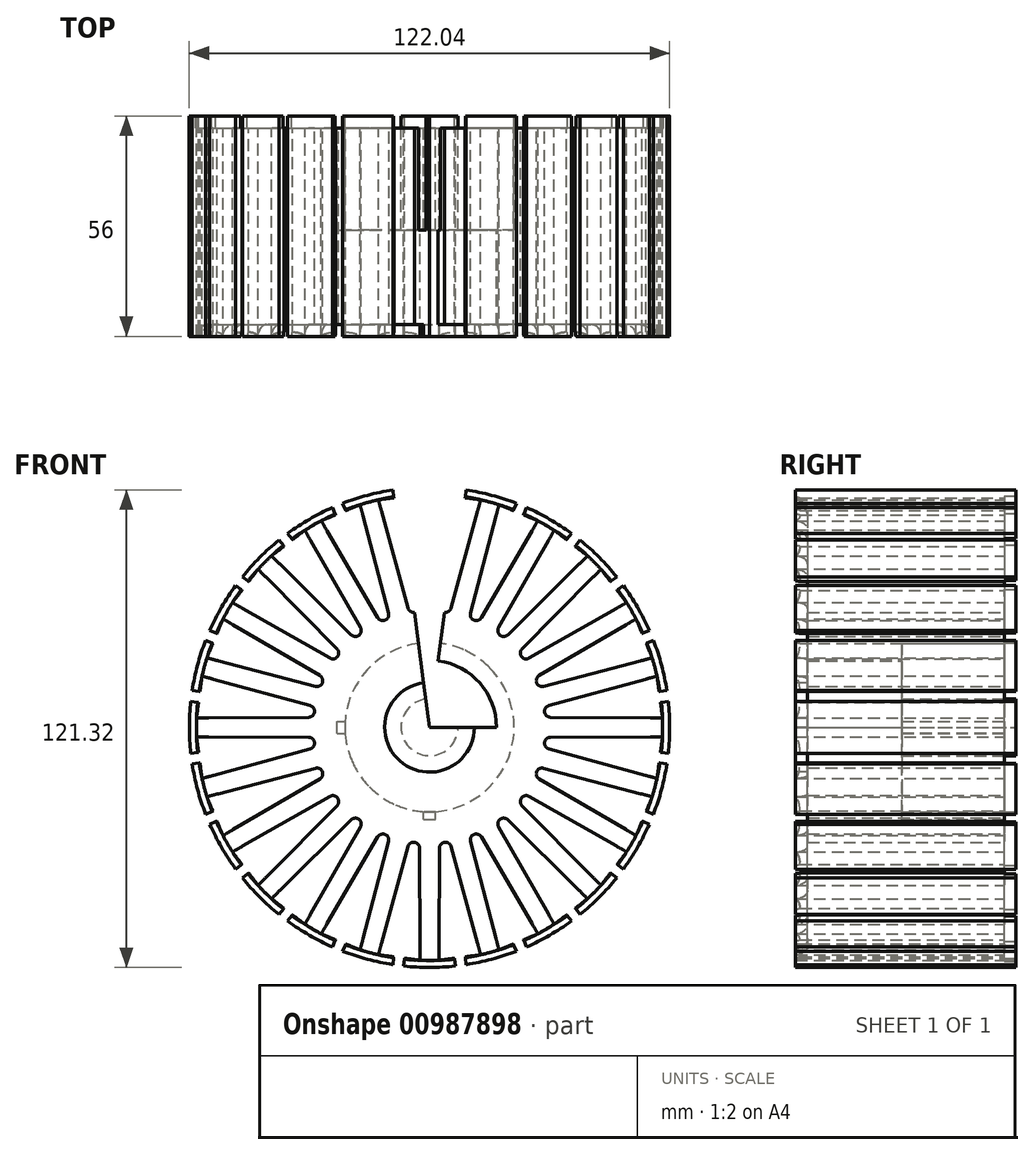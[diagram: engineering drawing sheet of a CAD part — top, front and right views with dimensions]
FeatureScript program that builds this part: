
annotation { "Feature Type Name" : "Feature", "Feature Type Description" : "" }
export const myFeature = defineFeature(function(context is Context, id is Id, definition is map)
    precondition{}
    {
        {
            var Q0;
            Q0=qCreatedBy(makeId("Front.planeOp"),FACE);
            var sketch = newSketch(context, id + "F0", { "sketchPlane" : qUnion([Q0])});
            skCircle(sketch, "E0", {"center": v(0, 0) * mm, "radius": 17 * mm});
            skLineSegment(sketch, "E1", {"start": v(0, 0) * mm, "end": v(0, 0) * mm});
            skLineSegment(sketch, "E2.MirrorCS", {"start": v(-63, 0) * mm, "end": v(-17, 0) * mm});
            skLineSegment(sketch, "E3.MirrorCS", {"start": v(-61, 5.5) * mm, "end": v(-30.77, 1.49) * mm});
            skLineSegment(sketch, "E4.MirrorCS", {"start": v(-61, -5.5) * mm, "end": v(-30.77, -1.49) * mm});
            skArc(sketch, "E5.MirrorCS", {"start": v(-30.77, 1.49) * mm, "mid": v(-29.47, 0) * mm, "end": v(-30.77, -1.49) * mm});
            skLineSegment(sketch, "E6.MirrorCS", {"start": v(-61, 1.38) * mm, "end": v(-61, 5.5) * mm});
            skLineSegment(sketch, "E7.MirrorCS", {"start": v(-63, 1.38) * mm, "end": v(-61, 1.38) * mm});
            skLineSegment(sketch, "E8.MirrorCS", {"start": v(-63, -1.38) * mm, "end": v(-61, -1.38) * mm});
            skLineSegment(sketch, "E9.MirrorCS", {"start": v(-61, -1.38) * mm, "end": v(-61, -5.5) * mm});
            skText(sketch, "E10", { "text": "correct", "fontName": "OpenSans-Regular.ttf"});
            skLineSegment(sketch, "E11.trimOffspring", {"start": v(-17, 0) * mm, "end": v(-26.3, 0) * mm});
            skLineSegment(sketch, "E12", {"start": v(0, 0) * mm, "end": v(54.99, 0) * mm});
            skLineSegment(sketch, "E13.MirrorCS", {"start": v(60.3, 9.33) * mm, "end": v(59.78, 13.26) * mm});
            skLineSegment(sketch, "E14.MirrorCS", {"start": v(60.66, 6.6) * mm, "end": v(61.17, 2.66) * mm});
            skLineSegment(sketch, "E15.MirrorCS", {"start": v(61.17, 2.66) * mm, "end": v(30.7, 2.54) * mm});
            skLineSegment(sketch, "E16.MirrorCS", {"start": v(59.78, 13.26) * mm, "end": v(30.32, 5.5) * mm});
            skArc(sketch, "E17.MirrorCS", {"start": v(30.32, 5.5) * mm, "mid": v(29.22, 3.85) * mm, "end": v(30.7, 2.54) * mm});
            skLineSegment(sketch, "E18.MirrorCS", {"start": v(62.46, 8.23) * mm, "end": v(0, 0) * mm});
            skLineSegment(sketch, "E19.MirrorCS", {"start": v(62.28, 9.6) * mm, "end": v(62.64, 6.86) * mm});
            skLineSegment(sketch, "E20.MirrorCS", {"start": v(62.64, 6.86) * mm, "end": v(60.66, 6.6) * mm});
            skLineSegment(sketch, "E21.MirrorCS", {"start": v(62.28, 9.6) * mm, "end": v(60.3, 9.33) * mm});
            skLineSegment(sketch, "E22.MirrorCS", {"start": v(0, 0) * mm, "end": v(-7.96, 60.48) * mm});
            skArc(sketch, "E23.MirrorCS", {"start": v(-5.5, 30.32) * mm, "mid": v(-3.85, 29.22) * mm, "end": v(-2.54, 30.71) * mm});
            skLineSegment(sketch, "E24.MirrorCS", {"start": v(-13, 57.8) * mm, "end": v(-5.5, 30.32) * mm});
            skLineSegment(sketch, "E25.MirrorCS", {"start": v(-2.4, 59.2) * mm, "end": v(-2.54, 30.71) * mm});
            skLineSegment(sketch, "E26.MirrorCS", {"start": v(-9.07, 58.32) * mm, "end": v(-13, 57.8) * mm});
            skLineSegment(sketch, "E27.MirrorCS", {"start": v(-9.33, 60.3) * mm, "end": v(-9.07, 58.32) * mm});
            skLineSegment(sketch, "E28.MirrorCS", {"start": v(-6.6, 60.66) * mm, "end": v(-6.33, 58.68) * mm});
            skLineSegment(sketch, "E29.MirrorCS", {"start": v(-6.33, 58.68) * mm, "end": v(-2.4, 59.2) * mm});
            skLineSegment(sketch, "E30", {"start": v(0, 50.95) * mm, "end": v(0, 0) * mm});
            skLineSegment(sketch, "E31.MirrorCS", {"start": v(2.4, 59.2) * mm, "end": v(2.54, 30.71) * mm});
            skArc(sketch, "E32.MirrorCS", {"start": v(5.5, 30.32) * mm, "mid": v(3.85, 29.22) * mm, "end": v(2.54, 30.71) * mm});
            skLineSegment(sketch, "E33.MirrorCS", {"start": v(0, 0) * mm, "end": v(7.96, 60.48) * mm});
            skLineSegment(sketch, "E34.MirrorCS", {"start": v(13, 57.8) * mm, "end": v(5.5, 30.32) * mm});
            skLineSegment(sketch, "E35.MirrorCS", {"start": v(6.33, 58.68) * mm, "end": v(2.4, 59.2) * mm});
            skLineSegment(sketch, "E36.MirrorCS", {"start": v(9.33, 60.3) * mm, "end": v(9.07, 58.32) * mm});
            skLineSegment(sketch, "E37.MirrorCS", {"start": v(9.07, 58.32) * mm, "end": v(13, 57.8) * mm});
            skLineSegment(sketch, "E38.MirrorCS", {"start": v(6.6, 60.66) * mm, "end": v(6.33, 58.68) * mm});
            skArc(sketch, "E39", {"start": v(-6.6, 60.66) * mm, "mid": v(0, 61.02) * mm, "end": v(6.6, 60.66) * mm});
            const initialGuessF0  = {"E10": [-0.06317, -0.01425, 1, 0, 0.0042]};
            skSetInitialGuess(sketch, initialGuessF0);
            skSolve(sketch);
        }
        {
            var Q0;
            {var subQ0=sQuery(id+"F0.wireOp",EDGE,"E33.MirrorCS");var subQ1=sQuery(id+"F0.wireOp",EDGE,"E0");var subQ2=makeQuery(id+"F0.imprint","INTERSECT",VERTEX,{"derivedFrom":[subQ1,subQ0]});Q0=makeQuery(id+"F0.imprint","IMPRINT",FACE,{"disambiguationData":[TD([[makeQuery(id+"F0.imprint","IMPRINT",EDGE,{"disambiguationData":[TD([[subQ2,-1.0]])],"derivedFrom":subQ1}),-1.0]])]});}
            var Q1;
            {var subQ0=sQuery(id+"F0.wireOp",EDGE,"E30");var subQ1=sQuery(id+"F0.wireOp",EDGE,"E0");var subQ2=makeQuery(id+"F0.imprint","INTERSECT",VERTEX,{"derivedFrom":[subQ1,subQ0]});Q1=makeQuery(id+"F0.imprint","IMPRINT",FACE,{"disambiguationData":[TD([[makeQuery(id+"F0.imprint","IMPRINT",EDGE,{"disambiguationData":[TD([[subQ2,-1.0]])],"derivedFrom":subQ1}),-1.0]])]});}
            var Q2;
            {var subQ0=sQuery(id+"F0.wireOp",EDGE,"E18.MirrorCS");var subQ1=sQuery(id+"F0.wireOp",EDGE,"E0");var subQ2=makeQuery(id+"F0.imprint","INTERSECT",VERTEX,{"derivedFrom":[subQ1,subQ0]});Q2=makeQuery(id+"F0.imprint","IMPRINT",FACE,{"disambiguationData":[TD([[makeQuery(id+"F0.imprint","IMPRINT",EDGE,{"disambiguationData":[TD([[subQ2,-1.0]])],"derivedFrom":subQ1}),-1.0]])]});}
            var Q3;
            {var subQ0=sQuery(id+"F0.wireOp",EDGE,"E22.MirrorCS");var subQ1=sQuery(id+"F0.wireOp",EDGE,"E0");var subQ2=makeQuery(id+"F0.imprint","INTERSECT",VERTEX,{"derivedFrom":[subQ1,subQ0]});Q3=makeQuery(id+"F0.imprint","IMPRINT",FACE,{"disambiguationData":[TD([[makeQuery(id+"F0.imprint","IMPRINT",EDGE,{"disambiguationData":[TD([[subQ2,-1.0]])],"derivedFrom":subQ1}),-1.0]])]});}
            var Q4;
            {var subQ1=sQuery(id+"F0.wireOp",EDGE,"E0");var subQ5=makeQuery(id+"F0.imprint","INTERSECT",VERTEX,{"derivedFrom":[subQ1,sQuery(id+"F0.wireOp",EDGE,"E11.trimOffspring")]});Q4=makeQuery(id+"F0.imprint","IMPRINT",FACE,{"disambiguationData":[TD([[makeQuery(id+"F0.imprint","IMPRINT",EDGE,{"disambiguationData":[TD([[subQ5,1.0]])],"derivedFrom":subQ1}),1.0]])]});}
            var Q5;
            {var subQ7=sQuery(id+"F0.wireOp",EDGE,"E25.MirrorCS");Q5=makeQuery(id+"F0.imprint","IMPRINT",FACE,{"disambiguationData":[TD([[makeQuery(id+"F0.imprint","IMPRINT",EDGE,{"derivedFrom":subQ7}),1.0]])]});}
            extrude(context, id + "F1", {"entities" : qUnion([Q0, Q1, Q2, Q3, Q4, Q5]), "depth" : 56 * mm, "offsetDistance" : 25 * mm});
        }
        {
            var Q0;
            Q0=makeQuery(id+"F1.opExtrude","SWEPT_BODY",BODY,{"disambiguationData":[OSD([sQuery(id+"F0.wireOp",EDGE,"E0"),sQuery(id+"F0.wireOp",EDGE,"E22.MirrorCS"),sQuery(id+"F0.wireOp",EDGE,"E23.MirrorCS"),sQuery(id+"F0.wireOp",EDGE,"E25.MirrorCS"),sQuery(id+"F0.wireOp",EDGE,"E28.MirrorCS"),sQuery(id+"F0.wireOp",EDGE,"E29.MirrorCS"),sQuery(id+"F0.wireOp",EDGE,"E31.MirrorCS"),sQuery(id+"F0.wireOp",EDGE,"E32.MirrorCS"),sQuery(id+"F0.wireOp",EDGE,"E33.MirrorCS"),sQuery(id+"F0.wireOp",EDGE,"E35.MirrorCS"),sQuery(id+"F0.wireOp",EDGE,"E38.MirrorCS"),sQuery(id+"F0.wireOp",EDGE,"E39")])]});
            var Q1;
            {var subQ0=sQuery(id+"F0.wireOp",EDGE,"E0");var subQ1=makeQuery(id+"F0.imprint","INTERSECT",VERTEX,{"derivedFrom":[subQ0,sQuery(id+"F0.wireOp",EDGE,"E11.trimOffspring")]});Q1=makeQuery(id+"F1.opExtrude","SWEPT_FACE",FACE,{"disambiguationData":[OSD([subQ0]),TDD([makeQuery(id+"F0.imprint","IMPRINT",EDGE,{"disambiguationData":[TD([[subQ1,1.0]])],"derivedFrom":subQ0}),makeQuery(id+"F0.imprint","IMPRINT",EDGE,{"disambiguationData":[TD([[subQ1,-1.0]])],"derivedFrom":subQ0})])]});}
            circularPattern(context, id + "F2", {"entities" : qUnion([Q0]), "axis" : qUnion([Q1]), "angle" : 360 * degree, "instanceCount" : 24, "equalSpace" : true});
        }
        {
            var Q0;
            Q0=makeQuery(id+"F1.opExtrude","SWEPT_BODY",BODY,{"disambiguationData":[OSD([sQuery(id+"F0.wireOp",EDGE,"E0"),sQuery(id+"F0.wireOp",EDGE,"E22.MirrorCS"),sQuery(id+"F0.wireOp",EDGE,"E23.MirrorCS"),sQuery(id+"F0.wireOp",EDGE,"E25.MirrorCS"),sQuery(id+"F0.wireOp",EDGE,"E28.MirrorCS"),sQuery(id+"F0.wireOp",EDGE,"E29.MirrorCS"),sQuery(id+"F0.wireOp",EDGE,"E31.MirrorCS"),sQuery(id+"F0.wireOp",EDGE,"E32.MirrorCS"),sQuery(id+"F0.wireOp",EDGE,"E33.MirrorCS"),sQuery(id+"F0.wireOp",EDGE,"E35.MirrorCS"),sQuery(id+"F0.wireOp",EDGE,"E38.MirrorCS"),sQuery(id+"F0.wireOp",EDGE,"E39")])]});
            var Q1;
            Q1=makeQuery(id+"F2.opPattern","COPY",BODY,{"derivedFrom":makeQuery(id+"F1.opExtrude","SWEPT_BODY",BODY,{"disambiguationData":[OSD([sQuery(id+"F0.wireOp",EDGE,"E0"),sQuery(id+"F0.wireOp",EDGE,"E22.MirrorCS"),sQuery(id+"F0.wireOp",EDGE,"E23.MirrorCS"),sQuery(id+"F0.wireOp",EDGE,"E25.MirrorCS"),sQuery(id+"F0.wireOp",EDGE,"E28.MirrorCS"),sQuery(id+"F0.wireOp",EDGE,"E29.MirrorCS"),sQuery(id+"F0.wireOp",EDGE,"E31.MirrorCS"),sQuery(id+"F0.wireOp",EDGE,"E32.MirrorCS"),sQuery(id+"F0.wireOp",EDGE,"E33.MirrorCS"),sQuery(id+"F0.wireOp",EDGE,"E35.MirrorCS"),sQuery(id+"F0.wireOp",EDGE,"E38.MirrorCS"),sQuery(id+"F0.wireOp",EDGE,"E39")])]}),"instanceName":"3"});
            var Q2;
            Q2=makeQuery(id+"F2.opPattern","COPY",BODY,{"derivedFrom":makeQuery(id+"F1.opExtrude","SWEPT_BODY",BODY,{"disambiguationData":[OSD([sQuery(id+"F0.wireOp",EDGE,"E0"),sQuery(id+"F0.wireOp",EDGE,"E22.MirrorCS"),sQuery(id+"F0.wireOp",EDGE,"E23.MirrorCS"),sQuery(id+"F0.wireOp",EDGE,"E25.MirrorCS"),sQuery(id+"F0.wireOp",EDGE,"E28.MirrorCS"),sQuery(id+"F0.wireOp",EDGE,"E29.MirrorCS"),sQuery(id+"F0.wireOp",EDGE,"E31.MirrorCS"),sQuery(id+"F0.wireOp",EDGE,"E32.MirrorCS"),sQuery(id+"F0.wireOp",EDGE,"E33.MirrorCS"),sQuery(id+"F0.wireOp",EDGE,"E35.MirrorCS"),sQuery(id+"F0.wireOp",EDGE,"E38.MirrorCS"),sQuery(id+"F0.wireOp",EDGE,"E39")])]}),"instanceName":"4"});
            var Q3;
            Q3=makeQuery(id+"F2.opPattern","COPY",BODY,{"derivedFrom":makeQuery(id+"F1.opExtrude","SWEPT_BODY",BODY,{"disambiguationData":[OSD([sQuery(id+"F0.wireOp",EDGE,"E0"),sQuery(id+"F0.wireOp",EDGE,"E22.MirrorCS"),sQuery(id+"F0.wireOp",EDGE,"E23.MirrorCS"),sQuery(id+"F0.wireOp",EDGE,"E25.MirrorCS"),sQuery(id+"F0.wireOp",EDGE,"E28.MirrorCS"),sQuery(id+"F0.wireOp",EDGE,"E29.MirrorCS"),sQuery(id+"F0.wireOp",EDGE,"E31.MirrorCS"),sQuery(id+"F0.wireOp",EDGE,"E32.MirrorCS"),sQuery(id+"F0.wireOp",EDGE,"E33.MirrorCS"),sQuery(id+"F0.wireOp",EDGE,"E35.MirrorCS"),sQuery(id+"F0.wireOp",EDGE,"E38.MirrorCS"),sQuery(id+"F0.wireOp",EDGE,"E39")])]}),"instanceName":"5"});
            var Q4;
            Q4=makeQuery(id+"F2.opPattern","COPY",BODY,{"derivedFrom":makeQuery(id+"F1.opExtrude","SWEPT_BODY",BODY,{"disambiguationData":[OSD([sQuery(id+"F0.wireOp",EDGE,"E0"),sQuery(id+"F0.wireOp",EDGE,"E22.MirrorCS"),sQuery(id+"F0.wireOp",EDGE,"E23.MirrorCS"),sQuery(id+"F0.wireOp",EDGE,"E25.MirrorCS"),sQuery(id+"F0.wireOp",EDGE,"E28.MirrorCS"),sQuery(id+"F0.wireOp",EDGE,"E29.MirrorCS"),sQuery(id+"F0.wireOp",EDGE,"E31.MirrorCS"),sQuery(id+"F0.wireOp",EDGE,"E32.MirrorCS"),sQuery(id+"F0.wireOp",EDGE,"E33.MirrorCS"),sQuery(id+"F0.wireOp",EDGE,"E35.MirrorCS"),sQuery(id+"F0.wireOp",EDGE,"E38.MirrorCS"),sQuery(id+"F0.wireOp",EDGE,"E39")])]}),"instanceName":"6"});
            var Q5;
            Q5=makeQuery(id+"F2.opPattern","COPY",BODY,{"derivedFrom":makeQuery(id+"F1.opExtrude","SWEPT_BODY",BODY,{"disambiguationData":[OSD([sQuery(id+"F0.wireOp",EDGE,"E0"),sQuery(id+"F0.wireOp",EDGE,"E22.MirrorCS"),sQuery(id+"F0.wireOp",EDGE,"E23.MirrorCS"),sQuery(id+"F0.wireOp",EDGE,"E25.MirrorCS"),sQuery(id+"F0.wireOp",EDGE,"E28.MirrorCS"),sQuery(id+"F0.wireOp",EDGE,"E29.MirrorCS"),sQuery(id+"F0.wireOp",EDGE,"E31.MirrorCS"),sQuery(id+"F0.wireOp",EDGE,"E32.MirrorCS"),sQuery(id+"F0.wireOp",EDGE,"E33.MirrorCS"),sQuery(id+"F0.wireOp",EDGE,"E35.MirrorCS"),sQuery(id+"F0.wireOp",EDGE,"E38.MirrorCS"),sQuery(id+"F0.wireOp",EDGE,"E39")])]}),"instanceName":"8"});
            var Q6;
            Q6=makeQuery(id+"F2.opPattern","COPY",BODY,{"derivedFrom":makeQuery(id+"F1.opExtrude","SWEPT_BODY",BODY,{"disambiguationData":[OSD([sQuery(id+"F0.wireOp",EDGE,"E0"),sQuery(id+"F0.wireOp",EDGE,"E22.MirrorCS"),sQuery(id+"F0.wireOp",EDGE,"E23.MirrorCS"),sQuery(id+"F0.wireOp",EDGE,"E25.MirrorCS"),sQuery(id+"F0.wireOp",EDGE,"E28.MirrorCS"),sQuery(id+"F0.wireOp",EDGE,"E29.MirrorCS"),sQuery(id+"F0.wireOp",EDGE,"E31.MirrorCS"),sQuery(id+"F0.wireOp",EDGE,"E32.MirrorCS"),sQuery(id+"F0.wireOp",EDGE,"E33.MirrorCS"),sQuery(id+"F0.wireOp",EDGE,"E35.MirrorCS"),sQuery(id+"F0.wireOp",EDGE,"E38.MirrorCS"),sQuery(id+"F0.wireOp",EDGE,"E39")])]}),"instanceName":"9"});
            var Q7;
            Q7=makeQuery(id+"F2.opPattern","COPY",BODY,{"derivedFrom":makeQuery(id+"F1.opExtrude","SWEPT_BODY",BODY,{"disambiguationData":[OSD([sQuery(id+"F0.wireOp",EDGE,"E0"),sQuery(id+"F0.wireOp",EDGE,"E22.MirrorCS"),sQuery(id+"F0.wireOp",EDGE,"E23.MirrorCS"),sQuery(id+"F0.wireOp",EDGE,"E25.MirrorCS"),sQuery(id+"F0.wireOp",EDGE,"E28.MirrorCS"),sQuery(id+"F0.wireOp",EDGE,"E29.MirrorCS"),sQuery(id+"F0.wireOp",EDGE,"E31.MirrorCS"),sQuery(id+"F0.wireOp",EDGE,"E32.MirrorCS"),sQuery(id+"F0.wireOp",EDGE,"E33.MirrorCS"),sQuery(id+"F0.wireOp",EDGE,"E35.MirrorCS"),sQuery(id+"F0.wireOp",EDGE,"E38.MirrorCS"),sQuery(id+"F0.wireOp",EDGE,"E39")])]}),"instanceName":"10"});
            var Q8;
            Q8=makeQuery(id+"F2.opPattern","COPY",BODY,{"derivedFrom":makeQuery(id+"F1.opExtrude","SWEPT_BODY",BODY,{"disambiguationData":[OSD([sQuery(id+"F0.wireOp",EDGE,"E0"),sQuery(id+"F0.wireOp",EDGE,"E22.MirrorCS"),sQuery(id+"F0.wireOp",EDGE,"E23.MirrorCS"),sQuery(id+"F0.wireOp",EDGE,"E25.MirrorCS"),sQuery(id+"F0.wireOp",EDGE,"E28.MirrorCS"),sQuery(id+"F0.wireOp",EDGE,"E29.MirrorCS"),sQuery(id+"F0.wireOp",EDGE,"E31.MirrorCS"),sQuery(id+"F0.wireOp",EDGE,"E32.MirrorCS"),sQuery(id+"F0.wireOp",EDGE,"E33.MirrorCS"),sQuery(id+"F0.wireOp",EDGE,"E35.MirrorCS"),sQuery(id+"F0.wireOp",EDGE,"E38.MirrorCS"),sQuery(id+"F0.wireOp",EDGE,"E39")])]}),"instanceName":"11"});
            var Q9;
            Q9=makeQuery(id+"F2.opPattern","COPY",BODY,{"derivedFrom":makeQuery(id+"F1.opExtrude","SWEPT_BODY",BODY,{"disambiguationData":[OSD([sQuery(id+"F0.wireOp",EDGE,"E0"),sQuery(id+"F0.wireOp",EDGE,"E22.MirrorCS"),sQuery(id+"F0.wireOp",EDGE,"E23.MirrorCS"),sQuery(id+"F0.wireOp",EDGE,"E25.MirrorCS"),sQuery(id+"F0.wireOp",EDGE,"E28.MirrorCS"),sQuery(id+"F0.wireOp",EDGE,"E29.MirrorCS"),sQuery(id+"F0.wireOp",EDGE,"E31.MirrorCS"),sQuery(id+"F0.wireOp",EDGE,"E32.MirrorCS"),sQuery(id+"F0.wireOp",EDGE,"E33.MirrorCS"),sQuery(id+"F0.wireOp",EDGE,"E35.MirrorCS"),sQuery(id+"F0.wireOp",EDGE,"E38.MirrorCS"),sQuery(id+"F0.wireOp",EDGE,"E39")])]}),"instanceName":"13"});
            var Q10;
            Q10=makeQuery(id+"F2.opPattern","COPY",BODY,{"derivedFrom":makeQuery(id+"F1.opExtrude","SWEPT_BODY",BODY,{"disambiguationData":[OSD([sQuery(id+"F0.wireOp",EDGE,"E0"),sQuery(id+"F0.wireOp",EDGE,"E22.MirrorCS"),sQuery(id+"F0.wireOp",EDGE,"E23.MirrorCS"),sQuery(id+"F0.wireOp",EDGE,"E25.MirrorCS"),sQuery(id+"F0.wireOp",EDGE,"E28.MirrorCS"),sQuery(id+"F0.wireOp",EDGE,"E29.MirrorCS"),sQuery(id+"F0.wireOp",EDGE,"E31.MirrorCS"),sQuery(id+"F0.wireOp",EDGE,"E32.MirrorCS"),sQuery(id+"F0.wireOp",EDGE,"E33.MirrorCS"),sQuery(id+"F0.wireOp",EDGE,"E35.MirrorCS"),sQuery(id+"F0.wireOp",EDGE,"E38.MirrorCS"),sQuery(id+"F0.wireOp",EDGE,"E39")])]}),"instanceName":"14"});
            var Q11;
            Q11=makeQuery(id+"F2.opPattern","COPY",BODY,{"derivedFrom":makeQuery(id+"F1.opExtrude","SWEPT_BODY",BODY,{"disambiguationData":[OSD([sQuery(id+"F0.wireOp",EDGE,"E0"),sQuery(id+"F0.wireOp",EDGE,"E22.MirrorCS"),sQuery(id+"F0.wireOp",EDGE,"E23.MirrorCS"),sQuery(id+"F0.wireOp",EDGE,"E25.MirrorCS"),sQuery(id+"F0.wireOp",EDGE,"E28.MirrorCS"),sQuery(id+"F0.wireOp",EDGE,"E29.MirrorCS"),sQuery(id+"F0.wireOp",EDGE,"E31.MirrorCS"),sQuery(id+"F0.wireOp",EDGE,"E32.MirrorCS"),sQuery(id+"F0.wireOp",EDGE,"E33.MirrorCS"),sQuery(id+"F0.wireOp",EDGE,"E35.MirrorCS"),sQuery(id+"F0.wireOp",EDGE,"E38.MirrorCS"),sQuery(id+"F0.wireOp",EDGE,"E39")])]}),"instanceName":"15"});
            var Q12;
            Q12=makeQuery(id+"F2.opPattern","COPY",BODY,{"derivedFrom":makeQuery(id+"F1.opExtrude","SWEPT_BODY",BODY,{"disambiguationData":[OSD([sQuery(id+"F0.wireOp",EDGE,"E0"),sQuery(id+"F0.wireOp",EDGE,"E22.MirrorCS"),sQuery(id+"F0.wireOp",EDGE,"E23.MirrorCS"),sQuery(id+"F0.wireOp",EDGE,"E25.MirrorCS"),sQuery(id+"F0.wireOp",EDGE,"E28.MirrorCS"),sQuery(id+"F0.wireOp",EDGE,"E29.MirrorCS"),sQuery(id+"F0.wireOp",EDGE,"E31.MirrorCS"),sQuery(id+"F0.wireOp",EDGE,"E32.MirrorCS"),sQuery(id+"F0.wireOp",EDGE,"E33.MirrorCS"),sQuery(id+"F0.wireOp",EDGE,"E35.MirrorCS"),sQuery(id+"F0.wireOp",EDGE,"E38.MirrorCS"),sQuery(id+"F0.wireOp",EDGE,"E39")])]}),"instanceName":"16"});
            var Q13;
            Q13=makeQuery(id+"F2.opPattern","COPY",BODY,{"derivedFrom":makeQuery(id+"F1.opExtrude","SWEPT_BODY",BODY,{"disambiguationData":[OSD([sQuery(id+"F0.wireOp",EDGE,"E0"),sQuery(id+"F0.wireOp",EDGE,"E22.MirrorCS"),sQuery(id+"F0.wireOp",EDGE,"E23.MirrorCS"),sQuery(id+"F0.wireOp",EDGE,"E25.MirrorCS"),sQuery(id+"F0.wireOp",EDGE,"E28.MirrorCS"),sQuery(id+"F0.wireOp",EDGE,"E29.MirrorCS"),sQuery(id+"F0.wireOp",EDGE,"E31.MirrorCS"),sQuery(id+"F0.wireOp",EDGE,"E32.MirrorCS"),sQuery(id+"F0.wireOp",EDGE,"E33.MirrorCS"),sQuery(id+"F0.wireOp",EDGE,"E35.MirrorCS"),sQuery(id+"F0.wireOp",EDGE,"E38.MirrorCS"),sQuery(id+"F0.wireOp",EDGE,"E39")])]}),"instanceName":"19"});
            var Q14;
            Q14=makeQuery(id+"F2.opPattern","COPY",BODY,{"derivedFrom":makeQuery(id+"F1.opExtrude","SWEPT_BODY",BODY,{"disambiguationData":[OSD([sQuery(id+"F0.wireOp",EDGE,"E0"),sQuery(id+"F0.wireOp",EDGE,"E22.MirrorCS"),sQuery(id+"F0.wireOp",EDGE,"E23.MirrorCS"),sQuery(id+"F0.wireOp",EDGE,"E25.MirrorCS"),sQuery(id+"F0.wireOp",EDGE,"E28.MirrorCS"),sQuery(id+"F0.wireOp",EDGE,"E29.MirrorCS"),sQuery(id+"F0.wireOp",EDGE,"E31.MirrorCS"),sQuery(id+"F0.wireOp",EDGE,"E32.MirrorCS"),sQuery(id+"F0.wireOp",EDGE,"E33.MirrorCS"),sQuery(id+"F0.wireOp",EDGE,"E35.MirrorCS"),sQuery(id+"F0.wireOp",EDGE,"E38.MirrorCS"),sQuery(id+"F0.wireOp",EDGE,"E39")])]}),"instanceName":"20"});
            var Q15;
            Q15=makeQuery(id+"F2.opPattern","COPY",BODY,{"derivedFrom":makeQuery(id+"F1.opExtrude","SWEPT_BODY",BODY,{"disambiguationData":[OSD([sQuery(id+"F0.wireOp",EDGE,"E0"),sQuery(id+"F0.wireOp",EDGE,"E22.MirrorCS"),sQuery(id+"F0.wireOp",EDGE,"E23.MirrorCS"),sQuery(id+"F0.wireOp",EDGE,"E25.MirrorCS"),sQuery(id+"F0.wireOp",EDGE,"E28.MirrorCS"),sQuery(id+"F0.wireOp",EDGE,"E29.MirrorCS"),sQuery(id+"F0.wireOp",EDGE,"E31.MirrorCS"),sQuery(id+"F0.wireOp",EDGE,"E32.MirrorCS"),sQuery(id+"F0.wireOp",EDGE,"E33.MirrorCS"),sQuery(id+"F0.wireOp",EDGE,"E35.MirrorCS"),sQuery(id+"F0.wireOp",EDGE,"E38.MirrorCS"),sQuery(id+"F0.wireOp",EDGE,"E39")])]}),"instanceName":"22"});
            var Q16;
            Q16=makeQuery(id+"F2.opPattern","COPY",BODY,{"derivedFrom":makeQuery(id+"F1.opExtrude","SWEPT_BODY",BODY,{"disambiguationData":[OSD([sQuery(id+"F0.wireOp",EDGE,"E0"),sQuery(id+"F0.wireOp",EDGE,"E22.MirrorCS"),sQuery(id+"F0.wireOp",EDGE,"E23.MirrorCS"),sQuery(id+"F0.wireOp",EDGE,"E25.MirrorCS"),sQuery(id+"F0.wireOp",EDGE,"E28.MirrorCS"),sQuery(id+"F0.wireOp",EDGE,"E29.MirrorCS"),sQuery(id+"F0.wireOp",EDGE,"E31.MirrorCS"),sQuery(id+"F0.wireOp",EDGE,"E32.MirrorCS"),sQuery(id+"F0.wireOp",EDGE,"E33.MirrorCS"),sQuery(id+"F0.wireOp",EDGE,"E35.MirrorCS"),sQuery(id+"F0.wireOp",EDGE,"E38.MirrorCS"),sQuery(id+"F0.wireOp",EDGE,"E39")])]}),"instanceName":"21"});
            var Q17;
            Q17=makeQuery(id+"F2.opPattern","COPY",BODY,{"derivedFrom":makeQuery(id+"F1.opExtrude","SWEPT_BODY",BODY,{"disambiguationData":[OSD([sQuery(id+"F0.wireOp",EDGE,"E0"),sQuery(id+"F0.wireOp",EDGE,"E22.MirrorCS"),sQuery(id+"F0.wireOp",EDGE,"E23.MirrorCS"),sQuery(id+"F0.wireOp",EDGE,"E25.MirrorCS"),sQuery(id+"F0.wireOp",EDGE,"E28.MirrorCS"),sQuery(id+"F0.wireOp",EDGE,"E29.MirrorCS"),sQuery(id+"F0.wireOp",EDGE,"E31.MirrorCS"),sQuery(id+"F0.wireOp",EDGE,"E32.MirrorCS"),sQuery(id+"F0.wireOp",EDGE,"E33.MirrorCS"),sQuery(id+"F0.wireOp",EDGE,"E35.MirrorCS"),sQuery(id+"F0.wireOp",EDGE,"E38.MirrorCS"),sQuery(id+"F0.wireOp",EDGE,"E39")])]}),"instanceName":"23"});
            var Q18;
            Q18=makeQuery(id+"F2.opPattern","COPY",BODY,{"derivedFrom":makeQuery(id+"F1.opExtrude","SWEPT_BODY",BODY,{"disambiguationData":[OSD([sQuery(id+"F0.wireOp",EDGE,"E0"),sQuery(id+"F0.wireOp",EDGE,"E22.MirrorCS"),sQuery(id+"F0.wireOp",EDGE,"E23.MirrorCS"),sQuery(id+"F0.wireOp",EDGE,"E25.MirrorCS"),sQuery(id+"F0.wireOp",EDGE,"E28.MirrorCS"),sQuery(id+"F0.wireOp",EDGE,"E29.MirrorCS"),sQuery(id+"F0.wireOp",EDGE,"E31.MirrorCS"),sQuery(id+"F0.wireOp",EDGE,"E32.MirrorCS"),sQuery(id+"F0.wireOp",EDGE,"E33.MirrorCS"),sQuery(id+"F0.wireOp",EDGE,"E35.MirrorCS"),sQuery(id+"F0.wireOp",EDGE,"E38.MirrorCS"),sQuery(id+"F0.wireOp",EDGE,"E39")])]}),"instanceName":"7"});
            var Q19;
            Q19=makeQuery(id+"F2.opPattern","COPY",BODY,{"derivedFrom":makeQuery(id+"F1.opExtrude","SWEPT_BODY",BODY,{"disambiguationData":[OSD([sQuery(id+"F0.wireOp",EDGE,"E0"),sQuery(id+"F0.wireOp",EDGE,"E22.MirrorCS"),sQuery(id+"F0.wireOp",EDGE,"E23.MirrorCS"),sQuery(id+"F0.wireOp",EDGE,"E25.MirrorCS"),sQuery(id+"F0.wireOp",EDGE,"E28.MirrorCS"),sQuery(id+"F0.wireOp",EDGE,"E29.MirrorCS"),sQuery(id+"F0.wireOp",EDGE,"E31.MirrorCS"),sQuery(id+"F0.wireOp",EDGE,"E32.MirrorCS"),sQuery(id+"F0.wireOp",EDGE,"E33.MirrorCS"),sQuery(id+"F0.wireOp",EDGE,"E35.MirrorCS"),sQuery(id+"F0.wireOp",EDGE,"E38.MirrorCS"),sQuery(id+"F0.wireOp",EDGE,"E39")])]}),"instanceName":"12"});
            var Q20;
            Q20=makeQuery(id+"F2.opPattern","COPY",BODY,{"derivedFrom":makeQuery(id+"F1.opExtrude","SWEPT_BODY",BODY,{"disambiguationData":[OSD([sQuery(id+"F0.wireOp",EDGE,"E0"),sQuery(id+"F0.wireOp",EDGE,"E22.MirrorCS"),sQuery(id+"F0.wireOp",EDGE,"E23.MirrorCS"),sQuery(id+"F0.wireOp",EDGE,"E25.MirrorCS"),sQuery(id+"F0.wireOp",EDGE,"E28.MirrorCS"),sQuery(id+"F0.wireOp",EDGE,"E29.MirrorCS"),sQuery(id+"F0.wireOp",EDGE,"E31.MirrorCS"),sQuery(id+"F0.wireOp",EDGE,"E32.MirrorCS"),sQuery(id+"F0.wireOp",EDGE,"E33.MirrorCS"),sQuery(id+"F0.wireOp",EDGE,"E35.MirrorCS"),sQuery(id+"F0.wireOp",EDGE,"E38.MirrorCS"),sQuery(id+"F0.wireOp",EDGE,"E39")])]}),"instanceName":"17"});
            var Q21;
            Q21=makeQuery(id+"F2.opPattern","COPY",BODY,{"derivedFrom":makeQuery(id+"F1.opExtrude","SWEPT_BODY",BODY,{"disambiguationData":[OSD([sQuery(id+"F0.wireOp",EDGE,"E0"),sQuery(id+"F0.wireOp",EDGE,"E22.MirrorCS"),sQuery(id+"F0.wireOp",EDGE,"E23.MirrorCS"),sQuery(id+"F0.wireOp",EDGE,"E25.MirrorCS"),sQuery(id+"F0.wireOp",EDGE,"E28.MirrorCS"),sQuery(id+"F0.wireOp",EDGE,"E29.MirrorCS"),sQuery(id+"F0.wireOp",EDGE,"E31.MirrorCS"),sQuery(id+"F0.wireOp",EDGE,"E32.MirrorCS"),sQuery(id+"F0.wireOp",EDGE,"E33.MirrorCS"),sQuery(id+"F0.wireOp",EDGE,"E35.MirrorCS"),sQuery(id+"F0.wireOp",EDGE,"E38.MirrorCS"),sQuery(id+"F0.wireOp",EDGE,"E39")])]}),"instanceName":"18"});
            var Q22;
            Q22=makeQuery(id+"F2.opPattern","COPY",BODY,{"derivedFrom":makeQuery(id+"F1.opExtrude","SWEPT_BODY",BODY,{"disambiguationData":[OSD([sQuery(id+"F0.wireOp",EDGE,"E0"),sQuery(id+"F0.wireOp",EDGE,"E22.MirrorCS"),sQuery(id+"F0.wireOp",EDGE,"E23.MirrorCS"),sQuery(id+"F0.wireOp",EDGE,"E25.MirrorCS"),sQuery(id+"F0.wireOp",EDGE,"E28.MirrorCS"),sQuery(id+"F0.wireOp",EDGE,"E29.MirrorCS"),sQuery(id+"F0.wireOp",EDGE,"E31.MirrorCS"),sQuery(id+"F0.wireOp",EDGE,"E32.MirrorCS"),sQuery(id+"F0.wireOp",EDGE,"E33.MirrorCS"),sQuery(id+"F0.wireOp",EDGE,"E35.MirrorCS"),sQuery(id+"F0.wireOp",EDGE,"E38.MirrorCS"),sQuery(id+"F0.wireOp",EDGE,"E39")])]}),"instanceName":"2"});
            var Q23;
            Q23=makeQuery(id+"F2.opPattern","COPY",BODY,{"derivedFrom":makeQuery(id+"F1.opExtrude","SWEPT_BODY",BODY,{"disambiguationData":[OSD([sQuery(id+"F0.wireOp",EDGE,"E0"),sQuery(id+"F0.wireOp",EDGE,"E22.MirrorCS"),sQuery(id+"F0.wireOp",EDGE,"E23.MirrorCS"),sQuery(id+"F0.wireOp",EDGE,"E25.MirrorCS"),sQuery(id+"F0.wireOp",EDGE,"E28.MirrorCS"),sQuery(id+"F0.wireOp",EDGE,"E29.MirrorCS"),sQuery(id+"F0.wireOp",EDGE,"E31.MirrorCS"),sQuery(id+"F0.wireOp",EDGE,"E32.MirrorCS"),sQuery(id+"F0.wireOp",EDGE,"E33.MirrorCS"),sQuery(id+"F0.wireOp",EDGE,"E35.MirrorCS"),sQuery(id+"F0.wireOp",EDGE,"E38.MirrorCS"),sQuery(id+"F0.wireOp",EDGE,"E39")])]}),"instanceName":"1"});
            booleanBodies(context, id + "F3", {"operationType" : BooleanOperationType.UNION, "tools" : qUnion([Q0, Q1, Q2, Q3, Q4, Q5, Q6, Q7, Q8, Q9, Q10, Q11, Q12, Q13, Q14, Q15, Q16, Q17, Q18, Q19, Q20, Q21, Q22, Q23])});
        }
        {
            var Q0;
            {var subQ1=sQuery(id+"F0.wireOp",EDGE,"E0");var subQ5=makeQuery(id+"F0.imprint","INTERSECT",VERTEX,{"derivedFrom":[subQ1,sQuery(id+"F0.wireOp",EDGE,"E11.trimOffspring")]});Q0=makeQuery(id+"F0.imprint","IMPRINT",FACE,{"disambiguationData":[TD([[makeQuery(id+"F0.imprint","IMPRINT",EDGE,{"disambiguationData":[TD([[subQ5,1.0]])],"derivedFrom":subQ1}),1.0]])]});}
            var Q1;
            {var subQ0=sQuery(id+"F0.wireOp",EDGE,"E33.MirrorCS");var subQ1=sQuery(id+"F0.wireOp",EDGE,"E0");var subQ2=makeQuery(id+"F0.imprint","INTERSECT",VERTEX,{"derivedFrom":[subQ1,subQ0]});Q1=makeQuery(id+"F0.imprint","IMPRINT",FACE,{"disambiguationData":[TD([[makeQuery(id+"F0.imprint","IMPRINT",EDGE,{"disambiguationData":[TD([[subQ2,-1.0]])],"derivedFrom":subQ1}),-1.0]])]});}
            var Q2;
            {var subQ0=sQuery(id+"F0.wireOp",EDGE,"E30");var subQ1=sQuery(id+"F0.wireOp",EDGE,"E0");var subQ2=makeQuery(id+"F0.imprint","INTERSECT",VERTEX,{"derivedFrom":[subQ1,subQ0]});Q2=makeQuery(id+"F0.imprint","IMPRINT",FACE,{"disambiguationData":[TD([[makeQuery(id+"F0.imprint","IMPRINT",EDGE,{"disambiguationData":[TD([[subQ2,-1.0]])],"derivedFrom":subQ1}),-1.0]])]});}
            var Q3;
            {var subQ0=sQuery(id+"F0.wireOp",EDGE,"E22.MirrorCS");var subQ1=sQuery(id+"F0.wireOp",EDGE,"E0");var subQ2=makeQuery(id+"F0.imprint","INTERSECT",VERTEX,{"derivedFrom":[subQ1,subQ0]});Q3=makeQuery(id+"F0.imprint","IMPRINT",FACE,{"disambiguationData":[TD([[makeQuery(id+"F0.imprint","IMPRINT",EDGE,{"disambiguationData":[TD([[subQ2,-1.0]])],"derivedFrom":subQ1}),-1.0]])]});}
            var Q4;
            {var subQ0=sQuery(id+"F0.wireOp",EDGE,"E18.MirrorCS");var subQ1=sQuery(id+"F0.wireOp",EDGE,"E0");var subQ2=makeQuery(id+"F0.imprint","INTERSECT",VERTEX,{"derivedFrom":[subQ1,subQ0]});Q4=makeQuery(id+"F0.imprint","IMPRINT",FACE,{"disambiguationData":[TD([[makeQuery(id+"F0.imprint","IMPRINT",EDGE,{"disambiguationData":[TD([[subQ2,-1.0]])],"derivedFrom":subQ1}),-1.0]])]});}
            extrude(context, id + "F4", {"entities" : qUnion([Q0, Q1, Q2, Q3, Q4]), "operationType" : NewBodyOperationType.REMOVE, "depth" : 56 * mm, "offsetDistance" : 25 * mm});
        }
        {
            var Q0;
            Q0=qCreatedBy(makeId("Front.planeOp"),FACE);
            var sketch = newSketch(context, id + "F5", { "sketchPlane" : qUnion([Q0])});
            skLineSegment(sketch, "E40", {"start": v(-1.5, 23.45) * mm, "end": v(-1.5, 21.45) * mm});
            skLineSegment(sketch, "E41", {"start": v(-1.5, 21.45) * mm, "end": v(-1.5, 21.45) * mm});
            skLineSegment(sketch, "E42.MirrorCS", {"start": v(1.5, 23.45) * mm, "end": v(1.5, 21.45) * mm});
            skLineSegment(sketch, "E43", {"start": v(1.5, 23.45) * mm, "end": v(-1.5, 23.45) * mm});
            skCircle(sketch, "E44", {"center": v(0, 0) * mm, "radius": 7.22 * mm});
            skArc(sketch, "E45", {"start": v(15.2, 15.2) * mm, "mid": v(-7.53, 20.14) * mm, "end": v(-21.45, 1.5) * mm});
            skLineSegment(sketch, "E46", {"start": v(-1.5, 21.45) * mm, "end": v(1.5, 21.45) * mm});
            skArc(sketch, "E47.trimOffspring", {"start": v(-21.45, -1.5) * mm, "mid": v(-19.56, -8.92) * mm, "end": v(-15.2, -15.2) * mm});
            skArc(sketch, "E48.MirrorCS", {"start": v(-15.2, -15.2) * mm, "mid": v(-20.14, 7.53) * mm, "end": v(-1.5, 21.45) * mm});
            skLineSegment(sketch, "E49.MirrorCS", {"start": v(-21.45, 1.5) * mm, "end": v(-21.45, -1.5) * mm});
            skLineSegment(sketch, "E50.MirrorCS", {"start": v(-23.45, -1.5) * mm, "end": v(-21.45, -1.5) * mm});
            skLineSegment(sketch, "E51.MirrorCS", {"start": v(-21.45, 1.5) * mm, "end": v(-21.45, 1.5) * mm});
            skLineSegment(sketch, "E52.MirrorCS", {"start": v(-23.45, -1.5) * mm, "end": v(-23.45, 1.5) * mm});
            skLineSegment(sketch, "E53.MirrorCS", {"start": v(-23.45, 1.5) * mm, "end": v(-21.45, 1.5) * mm});
            skArc(sketch, "E54.MirrorCS", {"start": v(1.5, 21.45) * mm, "mid": v(8.92, 19.56) * mm, "end": v(15.2, 15.2) * mm});
            skArc(sketch, "E55.trimOffspring", {"start": v(-15.2, -15.2) * mm, "mid": v(-19.56, -8.92) * mm, "end": v(-21.45, -1.5) * mm});
            skArc(sketch, "E56.MirrorCS", {"start": v(-15.2, -15.2) * mm, "mid": v(-8.92, -19.56) * mm, "end": v(-1.5, -21.45) * mm});
            skArc(sketch, "E57.MirrorCS", {"start": v(15.2, 15.2) * mm, "mid": v(20.14, -7.53) * mm, "end": v(1.5, -21.45) * mm});
            skLineSegment(sketch, "E58.MirrorCS", {"start": v(1.5, -21.45) * mm, "end": v(-1.5, -21.45) * mm});
            skArc(sketch, "E59.MirrorCS", {"start": v(-15.2, -15.2) * mm, "mid": v(7.53, -20.14) * mm, "end": v(21.45, -1.5) * mm});
            skLineSegment(sketch, "E60.MirrorCS", {"start": v(-1.5, -23.45) * mm, "end": v(-1.5, -21.45) * mm});
            skLineSegment(sketch, "E61.MirrorCS", {"start": v(-1.5, -23.45) * mm, "end": v(1.5, -23.45) * mm});
            skLineSegment(sketch, "E62.MirrorCS", {"start": v(1.5, -23.45) * mm, "end": v(1.5, -21.45) * mm});
            skLineSegment(sketch, "E63.MirrorCS", {"start": v(23.45, 1.5) * mm, "end": v(21.45, 1.5) * mm});
            skLineSegment(sketch, "E64.MirrorCS", {"start": v(23.45, 1.5) * mm, "end": v(23.45, -1.5) * mm});
            skLineSegment(sketch, "E65.MirrorCS", {"start": v(23.45, -1.5) * mm, "end": v(21.45, -1.5) * mm});
            skSolve(sketch);
        }
        {
            var Q0;
            Q0 = qSketchRegion(id + "F5", true);
            extrude(context, id + "F6", {"entities" : qUnion([Q0]), "operationType" : NewBodyOperationType.REMOVE, "depth" : 29 * mm, "offsetDistance" : 25 * mm});
        }
        {
            var Q0;
            Q0=qCreatedBy(makeId("Front.planeOp"),FACE);
            var sketch = newSketch(context, id + "F7", { "sketchPlane" : qUnion([Q0])});
            skCircle(sketch, "E66", {"center": v(0, 0) * mm, "radius": 59.43 * mm});
            skCircle(sketch, "E67", {"center": v(0, 0) * mm, "radius": 8.06 * mm});
            skSolve(sketch);
        }
        {
            var Q0;
            Q0=makeQuery(id+"F7.imprint","IMPRINT",FACE,{"disambiguationData":[TD([[makeQuery(id+"F7.imprint","IMPRINT",EDGE,{"derivedFrom":sQuery(id+"F7.wireOp",EDGE,"E66")}),1.0]])]});
            extrude(context, id + "F8", {"entities" : qUnion([Q0]), "operationType" : NewBodyOperationType.REMOVE, "depth" : 3 * mm, "offsetDistance" : 25 * mm});
        }
        {
            var Q0;
            {var subQ0=makeQuery(id+"F1.opExtrude","CAP_FACE",FACE,{"disambiguationData":[OSD([sQuery(id+"F0.wireOp",EDGE,"E0"),sQuery(id+"F0.wireOp",EDGE,"E22.MirrorCS"),sQuery(id+"F0.wireOp",EDGE,"E23.MirrorCS"),sQuery(id+"F0.wireOp",EDGE,"E25.MirrorCS"),sQuery(id+"F0.wireOp",EDGE,"E28.MirrorCS"),sQuery(id+"F0.wireOp",EDGE,"E29.MirrorCS"),sQuery(id+"F0.wireOp",EDGE,"E31.MirrorCS"),sQuery(id+"F0.wireOp",EDGE,"E32.MirrorCS"),sQuery(id+"F0.wireOp",EDGE,"E33.MirrorCS"),sQuery(id+"F0.wireOp",EDGE,"E35.MirrorCS"),sQuery(id+"F0.wireOp",EDGE,"E38.MirrorCS"),sQuery(id+"F0.wireOp",EDGE,"E39")])],"isStart":false});Q0=makeQuery(id+"F3.opBoolean","MERGE",FACE,{"derivedFrom":[subQ0,makeQuery(id+"F2.opPattern","COPY",FACE,{"derivedFrom":subQ0,"instanceName":"1"}),makeQuery(id+"F2.opPattern","COPY",FACE,{"derivedFrom":subQ0,"instanceName":"2"}),makeQuery(id+"F2.opPattern","COPY",FACE,{"derivedFrom":subQ0,"instanceName":"3"}),makeQuery(id+"F2.opPattern","COPY",FACE,{"derivedFrom":subQ0,"instanceName":"4"}),makeQuery(id+"F2.opPattern","COPY",FACE,{"derivedFrom":subQ0,"instanceName":"5"}),makeQuery(id+"F2.opPattern","COPY",FACE,{"derivedFrom":subQ0,"instanceName":"6"}),makeQuery(id+"F2.opPattern","COPY",FACE,{"derivedFrom":subQ0,"instanceName":"7"}),makeQuery(id+"F2.opPattern","COPY",FACE,{"derivedFrom":subQ0,"instanceName":"8"}),makeQuery(id+"F2.opPattern","COPY",FACE,{"derivedFrom":subQ0,"instanceName":"9"}),makeQuery(id+"F2.opPattern","COPY",FACE,{"derivedFrom":subQ0,"instanceName":"10"}),makeQuery(id+"F2.opPattern","COPY",FACE,{"derivedFrom":subQ0,"instanceName":"11"}),makeQuery(id+"F2.opPattern","COPY",FACE,{"derivedFrom":subQ0,"instanceName":"12"}),makeQuery(id+"F2.opPattern","COPY",FACE,{"derivedFrom":subQ0,"instanceName":"13"}),makeQuery(id+"F2.opPattern","COPY",FACE,{"derivedFrom":subQ0,"instanceName":"14"}),makeQuery(id+"F2.opPattern","COPY",FACE,{"derivedFrom":subQ0,"instanceName":"15"}),makeQuery(id+"F2.opPattern","COPY",FACE,{"derivedFrom":subQ0,"instanceName":"16"}),makeQuery(id+"F2.opPattern","COPY",FACE,{"derivedFrom":subQ0,"instanceName":"17"}),makeQuery(id+"F2.opPattern","COPY",FACE,{"derivedFrom":subQ0,"instanceName":"18"}),makeQuery(id+"F2.opPattern","COPY",FACE,{"derivedFrom":subQ0,"instanceName":"19"}),makeQuery(id+"F2.opPattern","COPY",FACE,{"derivedFrom":subQ0,"instanceName":"20"}),makeQuery(id+"F2.opPattern","COPY",FACE,{"derivedFrom":subQ0,"instanceName":"21"}),makeQuery(id+"F2.opPattern","COPY",FACE,{"derivedFrom":subQ0,"instanceName":"22"}),makeQuery(id+"F2.opPattern","COPY",FACE,{"derivedFrom":subQ0,"instanceName":"23"})]});}
            var sketch = newSketch(context, id + "F9", { "sketchPlane" : qUnion([Q0])});
            skCircle(sketch, "E68", {"center": v(0, 0) * mm, "radius": 11.4 * mm});
            skCircle(sketch, "E69", {"center": v(0, 0) * mm, "radius": 59.24 * mm});
            skSolve(sketch);
        }
        {
            var Q0;
            Q0 = qSketchRegion(id + "F9", true);
            extrude(context, id + "F10", {"entities" : qUnion([Q0]), "operationType" : NewBodyOperationType.REMOVE, "oppositeDirection" : true, "depth" : 3 * mm, "offsetDistance" : 25 * mm});
        }
        {
            var Q0;
            {var subQ0=sQuery(id+"F9.wireOp",EDGE,"E69");Q0=makeQuery(id+"F10.boolean.opBoolean","COPY",EDGE,{"disambiguationData":[TD([makeQuery(id+"F2.opPattern","COPY",FACE,{"derivedFrom":makeQuery(id+"F1.opExtrude","SWEPT_FACE",FACE,{"disambiguationData":[OSD([sQuery(id+"F0.wireOp",EDGE,"E28.MirrorCS")])]}),"instanceName":"22"}),makeQuery(id+"F2.opPattern","COPY",FACE,{"derivedFrom":makeQuery(id+"F1.opExtrude","SWEPT_FACE",FACE,{"disambiguationData":[OSD([sQuery(id+"F0.wireOp",EDGE,"E38.MirrorCS")])]}),"instanceName":"22"}),makeQuery(id+"F10.opExtrude","CAP_FACE",FACE,{"disambiguationData":[OSD([sQuery(id+"F9.wireOp",EDGE,"E68"),subQ0])],"isStart":false}),makeQuery(id+"F10.opExtrude","SWEPT_FACE",FACE,{"disambiguationData":[OSD([subQ0])]})])],"derivedFrom":makeQuery(id+"F10.opExtrude","CAP_EDGE",EDGE,{"disambiguationData":[OSD([subQ0])],"isStart":false})});}
            fillet(context, id + "F11", {"entities" : qUnion([Q0]), "radius" : 3 * mm, "tangentPropagation" : true, "allowEdgeOverflow" : false});
        }
        {
            var Q0;
            {var subQ0=sQuery(id+"F9.wireOp",EDGE,"E69");Q0=makeQuery(id+"F10.boolean.opBoolean","COPY",EDGE,{"disambiguationData":[TD([makeQuery(id+"F2.opPattern","COPY",FACE,{"derivedFrom":makeQuery(id+"F1.opExtrude","SWEPT_FACE",FACE,{"disambiguationData":[OSD([sQuery(id+"F0.wireOp",EDGE,"E28.MirrorCS")])]}),"instanceName":"11"}),makeQuery(id+"F2.opPattern","COPY",FACE,{"derivedFrom":makeQuery(id+"F1.opExtrude","SWEPT_FACE",FACE,{"disambiguationData":[OSD([sQuery(id+"F0.wireOp",EDGE,"E38.MirrorCS")])]}),"instanceName":"11"}),makeQuery(id+"F10.opExtrude","CAP_FACE",FACE,{"disambiguationData":[OSD([sQuery(id+"F9.wireOp",EDGE,"E68"),subQ0])],"isStart":false}),makeQuery(id+"F10.opExtrude","SWEPT_FACE",FACE,{"disambiguationData":[OSD([subQ0])]})])],"derivedFrom":makeQuery(id+"F10.opExtrude","CAP_EDGE",EDGE,{"disambiguationData":[OSD([subQ0])],"isStart":false})});}
            var Q1;
            {var subQ0=sQuery(id+"F9.wireOp",EDGE,"E69");Q1=makeQuery(id+"F10.boolean.opBoolean","COPY",EDGE,{"disambiguationData":[TD([makeQuery(id+"F2.opPattern","COPY",FACE,{"derivedFrom":makeQuery(id+"F1.opExtrude","SWEPT_FACE",FACE,{"disambiguationData":[OSD([sQuery(id+"F0.wireOp",EDGE,"E28.MirrorCS")])]}),"instanceName":"9"}),makeQuery(id+"F2.opPattern","COPY",FACE,{"derivedFrom":makeQuery(id+"F1.opExtrude","SWEPT_FACE",FACE,{"disambiguationData":[OSD([sQuery(id+"F0.wireOp",EDGE,"E38.MirrorCS")])]}),"instanceName":"9"}),makeQuery(id+"F10.opExtrude","CAP_FACE",FACE,{"disambiguationData":[OSD([sQuery(id+"F9.wireOp",EDGE,"E68"),subQ0])],"isStart":false}),makeQuery(id+"F10.opExtrude","SWEPT_FACE",FACE,{"disambiguationData":[OSD([subQ0])]})])],"derivedFrom":makeQuery(id+"F10.opExtrude","CAP_EDGE",EDGE,{"disambiguationData":[OSD([subQ0])],"isStart":false})});}
            var Q2;
            {var subQ0=sQuery(id+"F9.wireOp",EDGE,"E69");Q2=makeQuery(id+"F10.boolean.opBoolean","COPY",EDGE,{"disambiguationData":[TD([makeQuery(id+"F2.opPattern","COPY",FACE,{"derivedFrom":makeQuery(id+"F1.opExtrude","SWEPT_FACE",FACE,{"disambiguationData":[OSD([sQuery(id+"F0.wireOp",EDGE,"E28.MirrorCS")])]}),"instanceName":"10"}),makeQuery(id+"F2.opPattern","COPY",FACE,{"derivedFrom":makeQuery(id+"F1.opExtrude","SWEPT_FACE",FACE,{"disambiguationData":[OSD([sQuery(id+"F0.wireOp",EDGE,"E38.MirrorCS")])]}),"instanceName":"10"}),makeQuery(id+"F10.opExtrude","CAP_FACE",FACE,{"disambiguationData":[OSD([sQuery(id+"F9.wireOp",EDGE,"E68"),subQ0])],"isStart":false}),makeQuery(id+"F10.opExtrude","SWEPT_FACE",FACE,{"disambiguationData":[OSD([subQ0])]})])],"derivedFrom":makeQuery(id+"F10.opExtrude","CAP_EDGE",EDGE,{"disambiguationData":[OSD([subQ0])],"isStart":false})});}
            var Q3;
            {var subQ0=sQuery(id+"F9.wireOp",EDGE,"E69");Q3=makeQuery(id+"F10.boolean.opBoolean","COPY",EDGE,{"disambiguationData":[TD([makeQuery(id+"F2.opPattern","COPY",FACE,{"derivedFrom":makeQuery(id+"F1.opExtrude","SWEPT_FACE",FACE,{"disambiguationData":[OSD([sQuery(id+"F0.wireOp",EDGE,"E28.MirrorCS")])]}),"instanceName":"15"}),makeQuery(id+"F2.opPattern","COPY",FACE,{"derivedFrom":makeQuery(id+"F1.opExtrude","SWEPT_FACE",FACE,{"disambiguationData":[OSD([sQuery(id+"F0.wireOp",EDGE,"E38.MirrorCS")])]}),"instanceName":"15"}),makeQuery(id+"F10.opExtrude","CAP_FACE",FACE,{"disambiguationData":[OSD([sQuery(id+"F9.wireOp",EDGE,"E68"),subQ0])],"isStart":false}),makeQuery(id+"F10.opExtrude","SWEPT_FACE",FACE,{"disambiguationData":[OSD([subQ0])]})])],"derivedFrom":makeQuery(id+"F10.opExtrude","CAP_EDGE",EDGE,{"disambiguationData":[OSD([subQ0])],"isStart":false})});}
            var Q4;
            {var subQ0=sQuery(id+"F9.wireOp",EDGE,"E69");Q4=makeQuery(id+"F10.boolean.opBoolean","COPY",EDGE,{"disambiguationData":[TD([makeQuery(id+"F2.opPattern","COPY",FACE,{"derivedFrom":makeQuery(id+"F1.opExtrude","SWEPT_FACE",FACE,{"disambiguationData":[OSD([sQuery(id+"F0.wireOp",EDGE,"E28.MirrorCS")])]}),"instanceName":"13"}),makeQuery(id+"F2.opPattern","COPY",FACE,{"derivedFrom":makeQuery(id+"F1.opExtrude","SWEPT_FACE",FACE,{"disambiguationData":[OSD([sQuery(id+"F0.wireOp",EDGE,"E38.MirrorCS")])]}),"instanceName":"13"}),makeQuery(id+"F10.opExtrude","CAP_FACE",FACE,{"disambiguationData":[OSD([sQuery(id+"F9.wireOp",EDGE,"E68"),subQ0])],"isStart":false}),makeQuery(id+"F10.opExtrude","SWEPT_FACE",FACE,{"disambiguationData":[OSD([subQ0])]})])],"derivedFrom":makeQuery(id+"F10.opExtrude","CAP_EDGE",EDGE,{"disambiguationData":[OSD([subQ0])],"isStart":false})});}
            var Q5;
            {var subQ0=sQuery(id+"F9.wireOp",EDGE,"E69");Q5=makeQuery(id+"F10.boolean.opBoolean","COPY",EDGE,{"disambiguationData":[TD([makeQuery(id+"F2.opPattern","COPY",FACE,{"derivedFrom":makeQuery(id+"F1.opExtrude","SWEPT_FACE",FACE,{"disambiguationData":[OSD([sQuery(id+"F0.wireOp",EDGE,"E28.MirrorCS")])]}),"instanceName":"14"}),makeQuery(id+"F2.opPattern","COPY",FACE,{"derivedFrom":makeQuery(id+"F1.opExtrude","SWEPT_FACE",FACE,{"disambiguationData":[OSD([sQuery(id+"F0.wireOp",EDGE,"E38.MirrorCS")])]}),"instanceName":"14"}),makeQuery(id+"F10.opExtrude","CAP_FACE",FACE,{"disambiguationData":[OSD([sQuery(id+"F9.wireOp",EDGE,"E68"),subQ0])],"isStart":false}),makeQuery(id+"F10.opExtrude","SWEPT_FACE",FACE,{"disambiguationData":[OSD([subQ0])]})])],"derivedFrom":makeQuery(id+"F10.opExtrude","CAP_EDGE",EDGE,{"disambiguationData":[OSD([subQ0])],"isStart":false})});}
            var Q6;
            {var subQ0=sQuery(id+"F9.wireOp",EDGE,"E69");Q6=makeQuery(id+"F10.boolean.opBoolean","COPY",EDGE,{"disambiguationData":[TD([makeQuery(id+"F2.opPattern","COPY",FACE,{"derivedFrom":makeQuery(id+"F1.opExtrude","SWEPT_FACE",FACE,{"disambiguationData":[OSD([sQuery(id+"F0.wireOp",EDGE,"E28.MirrorCS")])]}),"instanceName":"16"}),makeQuery(id+"F2.opPattern","COPY",FACE,{"derivedFrom":makeQuery(id+"F1.opExtrude","SWEPT_FACE",FACE,{"disambiguationData":[OSD([sQuery(id+"F0.wireOp",EDGE,"E38.MirrorCS")])]}),"instanceName":"16"}),makeQuery(id+"F10.opExtrude","CAP_FACE",FACE,{"disambiguationData":[OSD([sQuery(id+"F9.wireOp",EDGE,"E68"),subQ0])],"isStart":false}),makeQuery(id+"F10.opExtrude","SWEPT_FACE",FACE,{"disambiguationData":[OSD([subQ0])]})])],"derivedFrom":makeQuery(id+"F10.opExtrude","CAP_EDGE",EDGE,{"disambiguationData":[OSD([subQ0])],"isStart":false})});}
            var Q7;
            {var subQ0=sQuery(id+"F9.wireOp",EDGE,"E69");Q7=makeQuery(id+"F10.boolean.opBoolean","COPY",EDGE,{"disambiguationData":[TD([makeQuery(id+"F2.opPattern","COPY",FACE,{"derivedFrom":makeQuery(id+"F1.opExtrude","SWEPT_FACE",FACE,{"disambiguationData":[OSD([sQuery(id+"F0.wireOp",EDGE,"E28.MirrorCS")])]}),"instanceName":"12"}),makeQuery(id+"F2.opPattern","COPY",FACE,{"derivedFrom":makeQuery(id+"F1.opExtrude","SWEPT_FACE",FACE,{"disambiguationData":[OSD([sQuery(id+"F0.wireOp",EDGE,"E38.MirrorCS")])]}),"instanceName":"12"}),makeQuery(id+"F10.opExtrude","CAP_FACE",FACE,{"disambiguationData":[OSD([sQuery(id+"F9.wireOp",EDGE,"E68"),subQ0])],"isStart":false}),makeQuery(id+"F10.opExtrude","SWEPT_FACE",FACE,{"disambiguationData":[OSD([subQ0])]})])],"derivedFrom":makeQuery(id+"F10.opExtrude","CAP_EDGE",EDGE,{"disambiguationData":[OSD([subQ0])],"isStart":false})});}
            var Q8;
            {var subQ0=sQuery(id+"F9.wireOp",EDGE,"E69");Q8=makeQuery(id+"F10.boolean.opBoolean","COPY",EDGE,{"disambiguationData":[TD([makeQuery(id+"F2.opPattern","COPY",FACE,{"derivedFrom":makeQuery(id+"F1.opExtrude","SWEPT_FACE",FACE,{"disambiguationData":[OSD([sQuery(id+"F0.wireOp",EDGE,"E28.MirrorCS")])]}),"instanceName":"8"}),makeQuery(id+"F2.opPattern","COPY",FACE,{"derivedFrom":makeQuery(id+"F1.opExtrude","SWEPT_FACE",FACE,{"disambiguationData":[OSD([sQuery(id+"F0.wireOp",EDGE,"E38.MirrorCS")])]}),"instanceName":"8"}),makeQuery(id+"F10.opExtrude","CAP_FACE",FACE,{"disambiguationData":[OSD([sQuery(id+"F9.wireOp",EDGE,"E68"),subQ0])],"isStart":false}),makeQuery(id+"F10.opExtrude","SWEPT_FACE",FACE,{"disambiguationData":[OSD([subQ0])]})])],"derivedFrom":makeQuery(id+"F10.opExtrude","CAP_EDGE",EDGE,{"disambiguationData":[OSD([subQ0])],"isStart":false})});}
            var Q9;
            {var subQ0=sQuery(id+"F9.wireOp",EDGE,"E69");Q9=makeQuery(id+"F10.boolean.opBoolean","COPY",EDGE,{"disambiguationData":[TD([makeQuery(id+"F2.opPattern","COPY",FACE,{"derivedFrom":makeQuery(id+"F1.opExtrude","SWEPT_FACE",FACE,{"disambiguationData":[OSD([sQuery(id+"F0.wireOp",EDGE,"E28.MirrorCS")])]}),"instanceName":"7"}),makeQuery(id+"F2.opPattern","COPY",FACE,{"derivedFrom":makeQuery(id+"F1.opExtrude","SWEPT_FACE",FACE,{"disambiguationData":[OSD([sQuery(id+"F0.wireOp",EDGE,"E38.MirrorCS")])]}),"instanceName":"7"}),makeQuery(id+"F10.opExtrude","CAP_FACE",FACE,{"disambiguationData":[OSD([sQuery(id+"F9.wireOp",EDGE,"E68"),subQ0])],"isStart":false}),makeQuery(id+"F10.opExtrude","SWEPT_FACE",FACE,{"disambiguationData":[OSD([subQ0])]})])],"derivedFrom":makeQuery(id+"F10.opExtrude","CAP_EDGE",EDGE,{"disambiguationData":[OSD([subQ0])],"isStart":false})});}
            var Q10;
            {var subQ0=sQuery(id+"F9.wireOp",EDGE,"E69");Q10=makeQuery(id+"F10.boolean.opBoolean","COPY",EDGE,{"disambiguationData":[TD([makeQuery(id+"F2.opPattern","COPY",FACE,{"derivedFrom":makeQuery(id+"F1.opExtrude","SWEPT_FACE",FACE,{"disambiguationData":[OSD([sQuery(id+"F0.wireOp",EDGE,"E28.MirrorCS")])]}),"instanceName":"5"}),makeQuery(id+"F2.opPattern","COPY",FACE,{"derivedFrom":makeQuery(id+"F1.opExtrude","SWEPT_FACE",FACE,{"disambiguationData":[OSD([sQuery(id+"F0.wireOp",EDGE,"E38.MirrorCS")])]}),"instanceName":"5"}),makeQuery(id+"F10.opExtrude","CAP_FACE",FACE,{"disambiguationData":[OSD([sQuery(id+"F9.wireOp",EDGE,"E68"),subQ0])],"isStart":false}),makeQuery(id+"F10.opExtrude","SWEPT_FACE",FACE,{"disambiguationData":[OSD([subQ0])]})])],"derivedFrom":makeQuery(id+"F10.opExtrude","CAP_EDGE",EDGE,{"disambiguationData":[OSD([subQ0])],"isStart":false})});}
            var Q11;
            {var subQ0=sQuery(id+"F9.wireOp",EDGE,"E69");Q11=makeQuery(id+"F10.boolean.opBoolean","COPY",EDGE,{"disambiguationData":[TD([makeQuery(id+"F2.opPattern","COPY",FACE,{"derivedFrom":makeQuery(id+"F1.opExtrude","SWEPT_FACE",FACE,{"disambiguationData":[OSD([sQuery(id+"F0.wireOp",EDGE,"E28.MirrorCS")])]}),"instanceName":"4"}),makeQuery(id+"F2.opPattern","COPY",FACE,{"derivedFrom":makeQuery(id+"F1.opExtrude","SWEPT_FACE",FACE,{"disambiguationData":[OSD([sQuery(id+"F0.wireOp",EDGE,"E38.MirrorCS")])]}),"instanceName":"4"}),makeQuery(id+"F10.opExtrude","CAP_FACE",FACE,{"disambiguationData":[OSD([sQuery(id+"F9.wireOp",EDGE,"E68"),subQ0])],"isStart":false}),makeQuery(id+"F10.opExtrude","SWEPT_FACE",FACE,{"disambiguationData":[OSD([subQ0])]})])],"derivedFrom":makeQuery(id+"F10.opExtrude","CAP_EDGE",EDGE,{"disambiguationData":[OSD([subQ0])],"isStart":false})});}
            var Q12;
            {var subQ0=sQuery(id+"F9.wireOp",EDGE,"E69");Q12=makeQuery(id+"F10.boolean.opBoolean","COPY",EDGE,{"disambiguationData":[TD([makeQuery(id+"F2.opPattern","COPY",FACE,{"derivedFrom":makeQuery(id+"F1.opExtrude","SWEPT_FACE",FACE,{"disambiguationData":[OSD([sQuery(id+"F0.wireOp",EDGE,"E28.MirrorCS")])]}),"instanceName":"3"}),makeQuery(id+"F2.opPattern","COPY",FACE,{"derivedFrom":makeQuery(id+"F1.opExtrude","SWEPT_FACE",FACE,{"disambiguationData":[OSD([sQuery(id+"F0.wireOp",EDGE,"E38.MirrorCS")])]}),"instanceName":"3"}),makeQuery(id+"F10.opExtrude","CAP_FACE",FACE,{"disambiguationData":[OSD([sQuery(id+"F9.wireOp",EDGE,"E68"),subQ0])],"isStart":false}),makeQuery(id+"F10.opExtrude","SWEPT_FACE",FACE,{"disambiguationData":[OSD([subQ0])]})])],"derivedFrom":makeQuery(id+"F10.opExtrude","CAP_EDGE",EDGE,{"disambiguationData":[OSD([subQ0])],"isStart":false})});}
            var Q13;
            {var subQ0=sQuery(id+"F9.wireOp",EDGE,"E69");Q13=makeQuery(id+"F10.boolean.opBoolean","COPY",EDGE,{"disambiguationData":[TD([makeQuery(id+"F2.opPattern","COPY",FACE,{"derivedFrom":makeQuery(id+"F1.opExtrude","SWEPT_FACE",FACE,{"disambiguationData":[OSD([sQuery(id+"F0.wireOp",EDGE,"E28.MirrorCS")])]}),"instanceName":"2"}),makeQuery(id+"F2.opPattern","COPY",FACE,{"derivedFrom":makeQuery(id+"F1.opExtrude","SWEPT_FACE",FACE,{"disambiguationData":[OSD([sQuery(id+"F0.wireOp",EDGE,"E38.MirrorCS")])]}),"instanceName":"2"}),makeQuery(id+"F10.opExtrude","CAP_FACE",FACE,{"disambiguationData":[OSD([sQuery(id+"F9.wireOp",EDGE,"E68"),subQ0])],"isStart":false}),makeQuery(id+"F10.opExtrude","SWEPT_FACE",FACE,{"disambiguationData":[OSD([subQ0])]})])],"derivedFrom":makeQuery(id+"F10.opExtrude","CAP_EDGE",EDGE,{"disambiguationData":[OSD([subQ0])],"isStart":false})});}
            var Q14;
            {var subQ0=sQuery(id+"F9.wireOp",EDGE,"E69");Q14=makeQuery(id+"F10.boolean.opBoolean","COPY",EDGE,{"disambiguationData":[TD([makeQuery(id+"F1.opExtrude","SWEPT_FACE",FACE,{"disambiguationData":[OSD([sQuery(id+"F0.wireOp",EDGE,"E28.MirrorCS")])]}),makeQuery(id+"F1.opExtrude","SWEPT_FACE",FACE,{"disambiguationData":[OSD([sQuery(id+"F0.wireOp",EDGE,"E38.MirrorCS")])]}),makeQuery(id+"F10.opExtrude","CAP_FACE",FACE,{"disambiguationData":[OSD([sQuery(id+"F9.wireOp",EDGE,"E68"),subQ0])],"isStart":false}),makeQuery(id+"F10.opExtrude","SWEPT_FACE",FACE,{"disambiguationData":[OSD([subQ0])]})])],"derivedFrom":makeQuery(id+"F10.opExtrude","CAP_EDGE",EDGE,{"disambiguationData":[OSD([subQ0])],"isStart":false})});}
            var Q15;
            {var subQ0=sQuery(id+"F9.wireOp",EDGE,"E69");Q15=makeQuery(id+"F10.boolean.opBoolean","COPY",EDGE,{"disambiguationData":[TD([makeQuery(id+"F2.opPattern","COPY",FACE,{"derivedFrom":makeQuery(id+"F1.opExtrude","SWEPT_FACE",FACE,{"disambiguationData":[OSD([sQuery(id+"F0.wireOp",EDGE,"E28.MirrorCS")])]}),"instanceName":"23"}),makeQuery(id+"F2.opPattern","COPY",FACE,{"derivedFrom":makeQuery(id+"F1.opExtrude","SWEPT_FACE",FACE,{"disambiguationData":[OSD([sQuery(id+"F0.wireOp",EDGE,"E38.MirrorCS")])]}),"instanceName":"23"}),makeQuery(id+"F10.opExtrude","CAP_FACE",FACE,{"disambiguationData":[OSD([sQuery(id+"F9.wireOp",EDGE,"E68"),subQ0])],"isStart":false}),makeQuery(id+"F10.opExtrude","SWEPT_FACE",FACE,{"disambiguationData":[OSD([subQ0])]})])],"derivedFrom":makeQuery(id+"F10.opExtrude","CAP_EDGE",EDGE,{"disambiguationData":[OSD([subQ0])],"isStart":false})});}
            var Q16;
            {var subQ0=sQuery(id+"F9.wireOp",EDGE,"E69");Q16=makeQuery(id+"F10.boolean.opBoolean","COPY",EDGE,{"disambiguationData":[TD([makeQuery(id+"F2.opPattern","COPY",FACE,{"derivedFrom":makeQuery(id+"F1.opExtrude","SWEPT_FACE",FACE,{"disambiguationData":[OSD([sQuery(id+"F0.wireOp",EDGE,"E28.MirrorCS")])]}),"instanceName":"1"}),makeQuery(id+"F2.opPattern","COPY",FACE,{"derivedFrom":makeQuery(id+"F1.opExtrude","SWEPT_FACE",FACE,{"disambiguationData":[OSD([sQuery(id+"F0.wireOp",EDGE,"E38.MirrorCS")])]}),"instanceName":"1"}),makeQuery(id+"F10.opExtrude","CAP_FACE",FACE,{"disambiguationData":[OSD([sQuery(id+"F9.wireOp",EDGE,"E68"),subQ0])],"isStart":false}),makeQuery(id+"F10.opExtrude","SWEPT_FACE",FACE,{"disambiguationData":[OSD([subQ0])]})])],"derivedFrom":makeQuery(id+"F10.opExtrude","CAP_EDGE",EDGE,{"disambiguationData":[OSD([subQ0])],"isStart":false})});}
            var Q17;
            {var subQ0=sQuery(id+"F9.wireOp",EDGE,"E69");Q17=makeQuery(id+"F10.boolean.opBoolean","COPY",EDGE,{"disambiguationData":[TD([makeQuery(id+"F2.opPattern","COPY",FACE,{"derivedFrom":makeQuery(id+"F1.opExtrude","SWEPT_FACE",FACE,{"disambiguationData":[OSD([sQuery(id+"F0.wireOp",EDGE,"E28.MirrorCS")])]}),"instanceName":"18"}),makeQuery(id+"F2.opPattern","COPY",FACE,{"derivedFrom":makeQuery(id+"F1.opExtrude","SWEPT_FACE",FACE,{"disambiguationData":[OSD([sQuery(id+"F0.wireOp",EDGE,"E38.MirrorCS")])]}),"instanceName":"18"}),makeQuery(id+"F10.opExtrude","CAP_FACE",FACE,{"disambiguationData":[OSD([sQuery(id+"F9.wireOp",EDGE,"E68"),subQ0])],"isStart":false}),makeQuery(id+"F10.opExtrude","SWEPT_FACE",FACE,{"disambiguationData":[OSD([subQ0])]})])],"derivedFrom":makeQuery(id+"F10.opExtrude","CAP_EDGE",EDGE,{"disambiguationData":[OSD([subQ0])],"isStart":false})});}
            var Q18;
            {var subQ0=sQuery(id+"F9.wireOp",EDGE,"E69");Q18=makeQuery(id+"F10.boolean.opBoolean","COPY",EDGE,{"disambiguationData":[TD([makeQuery(id+"F2.opPattern","COPY",FACE,{"derivedFrom":makeQuery(id+"F1.opExtrude","SWEPT_FACE",FACE,{"disambiguationData":[OSD([sQuery(id+"F0.wireOp",EDGE,"E28.MirrorCS")])]}),"instanceName":"19"}),makeQuery(id+"F2.opPattern","COPY",FACE,{"derivedFrom":makeQuery(id+"F1.opExtrude","SWEPT_FACE",FACE,{"disambiguationData":[OSD([sQuery(id+"F0.wireOp",EDGE,"E38.MirrorCS")])]}),"instanceName":"19"}),makeQuery(id+"F10.opExtrude","CAP_FACE",FACE,{"disambiguationData":[OSD([sQuery(id+"F9.wireOp",EDGE,"E68"),subQ0])],"isStart":false}),makeQuery(id+"F10.opExtrude","SWEPT_FACE",FACE,{"disambiguationData":[OSD([subQ0])]})])],"derivedFrom":makeQuery(id+"F10.opExtrude","CAP_EDGE",EDGE,{"disambiguationData":[OSD([subQ0])],"isStart":false})});}
            var Q19;
            {var subQ0=sQuery(id+"F9.wireOp",EDGE,"E69");Q19=makeQuery(id+"F10.boolean.opBoolean","COPY",EDGE,{"disambiguationData":[TD([makeQuery(id+"F2.opPattern","COPY",FACE,{"derivedFrom":makeQuery(id+"F1.opExtrude","SWEPT_FACE",FACE,{"disambiguationData":[OSD([sQuery(id+"F0.wireOp",EDGE,"E28.MirrorCS")])]}),"instanceName":"20"}),makeQuery(id+"F2.opPattern","COPY",FACE,{"derivedFrom":makeQuery(id+"F1.opExtrude","SWEPT_FACE",FACE,{"disambiguationData":[OSD([sQuery(id+"F0.wireOp",EDGE,"E38.MirrorCS")])]}),"instanceName":"20"}),makeQuery(id+"F10.opExtrude","CAP_FACE",FACE,{"disambiguationData":[OSD([sQuery(id+"F9.wireOp",EDGE,"E68"),subQ0])],"isStart":false}),makeQuery(id+"F10.opExtrude","SWEPT_FACE",FACE,{"disambiguationData":[OSD([subQ0])]})])],"derivedFrom":makeQuery(id+"F10.opExtrude","CAP_EDGE",EDGE,{"disambiguationData":[OSD([subQ0])],"isStart":false})});}
            var Q20;
            {var subQ0=sQuery(id+"F9.wireOp",EDGE,"E69");Q20=makeQuery(id+"F10.boolean.opBoolean","COPY",EDGE,{"disambiguationData":[TD([makeQuery(id+"F2.opPattern","COPY",FACE,{"derivedFrom":makeQuery(id+"F1.opExtrude","SWEPT_FACE",FACE,{"disambiguationData":[OSD([sQuery(id+"F0.wireOp",EDGE,"E28.MirrorCS")])]}),"instanceName":"21"}),makeQuery(id+"F2.opPattern","COPY",FACE,{"derivedFrom":makeQuery(id+"F1.opExtrude","SWEPT_FACE",FACE,{"disambiguationData":[OSD([sQuery(id+"F0.wireOp",EDGE,"E38.MirrorCS")])]}),"instanceName":"21"}),makeQuery(id+"F10.opExtrude","CAP_FACE",FACE,{"disambiguationData":[OSD([sQuery(id+"F9.wireOp",EDGE,"E68"),subQ0])],"isStart":false}),makeQuery(id+"F10.opExtrude","SWEPT_FACE",FACE,{"disambiguationData":[OSD([subQ0])]})])],"derivedFrom":makeQuery(id+"F10.opExtrude","CAP_EDGE",EDGE,{"disambiguationData":[OSD([subQ0])],"isStart":false})});}
            fillet(context, id + "F12", {"entities" : qUnion([Q0, Q1, Q2, Q3, Q4, Q5, Q6, Q7, Q8, Q9, Q10, Q11, Q12, Q13, Q14, Q15, Q16, Q17, Q18, Q19, Q20]), "radius" : 3 * mm, "tangentPropagation" : true, "allowEdgeOverflow" : false});
        }
    });
